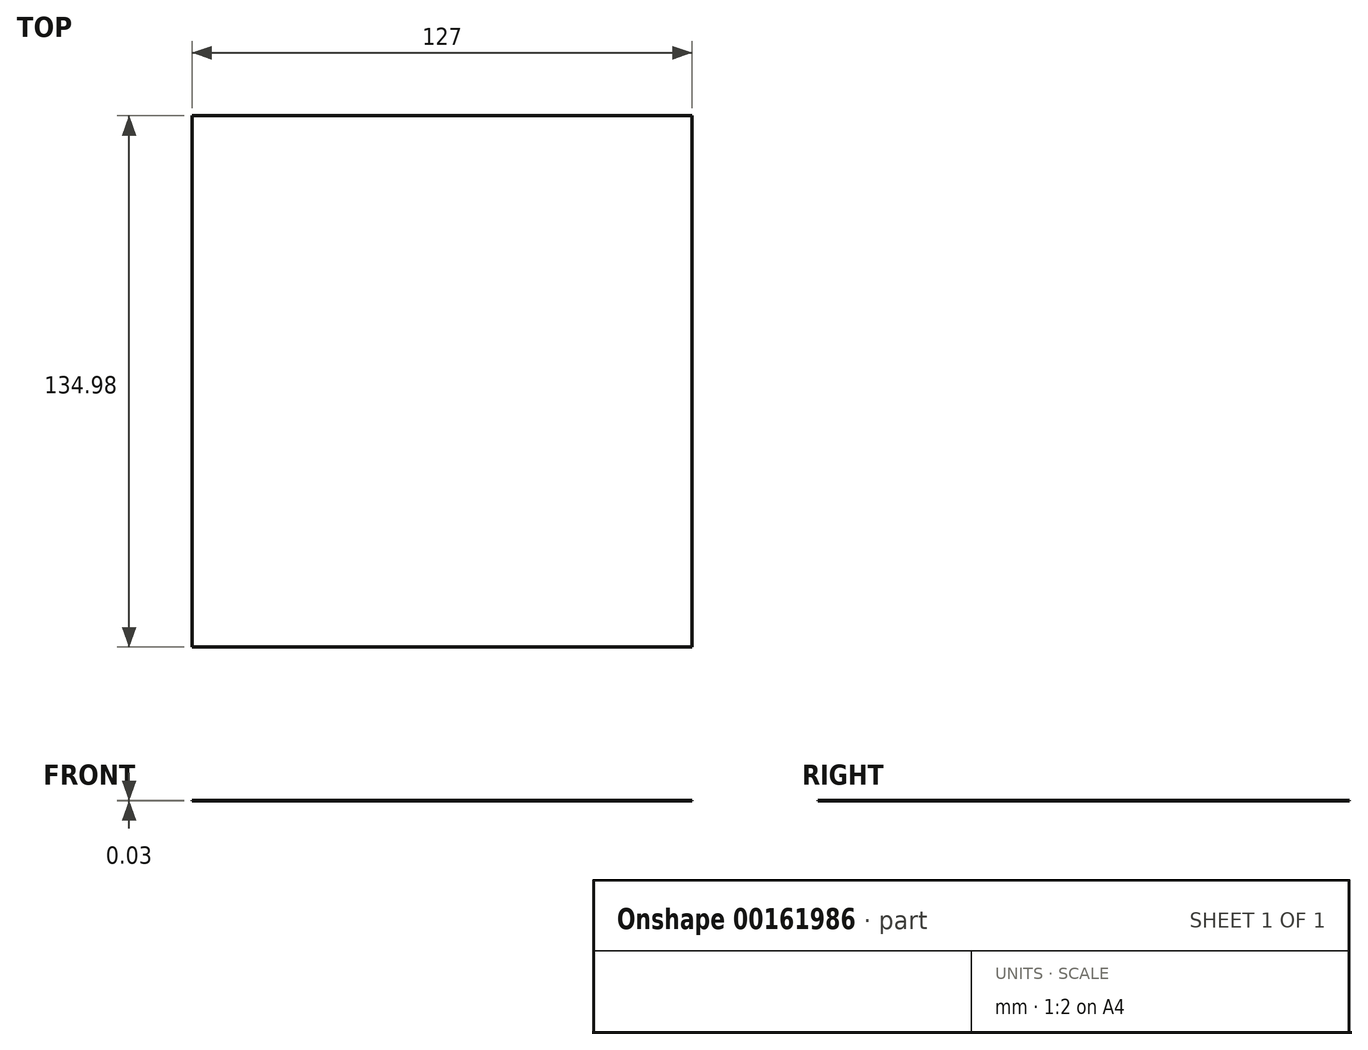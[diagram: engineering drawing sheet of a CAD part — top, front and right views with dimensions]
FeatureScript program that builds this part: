
annotation { "Feature Type Name" : "Feature", "Feature Type Description" : "" }
export const myFeature = defineFeature(function(context is Context, id is Id, definition is map)
    precondition{}
    {
        {
            var Q0;
            Q0=qCreatedBy(makeId("Top.planeOp"),FACE);
            var sketch = newSketch(context, id + "F0", { "sketchPlane" : qUnion([Q0])});
            skLineSegment(sketch, "E0.bottom", {"start": v(63.5, 67.49) * mm, "end": v(-63.5, 67.49) * mm});
            skLineSegment(sketch, "E0.top", {"start": v(63.5, -67.49) * mm, "end": v(-63.5, -67.49) * mm});
            skLineSegment(sketch, "E0.left", {"start": v(63.5, 67.49) * mm, "end": v(63.5, -67.49) * mm});
            skLineSegment(sketch, "E0.right", {"start": v(-63.5, 67.49) * mm, "end": v(-63.5, -67.49) * mm});
            skPoint(sketch, "E0.middle", {"position": v(0, 0) * mm});
            skSolve(sketch);
        }
        {
            var Q0;
            Q0 = qSketchRegion(id + "F0", true);
            extrude(context, id + "F1", {"entities" : qUnion([Q0]), "depth" : 0.03 * mm});
        }
    });
